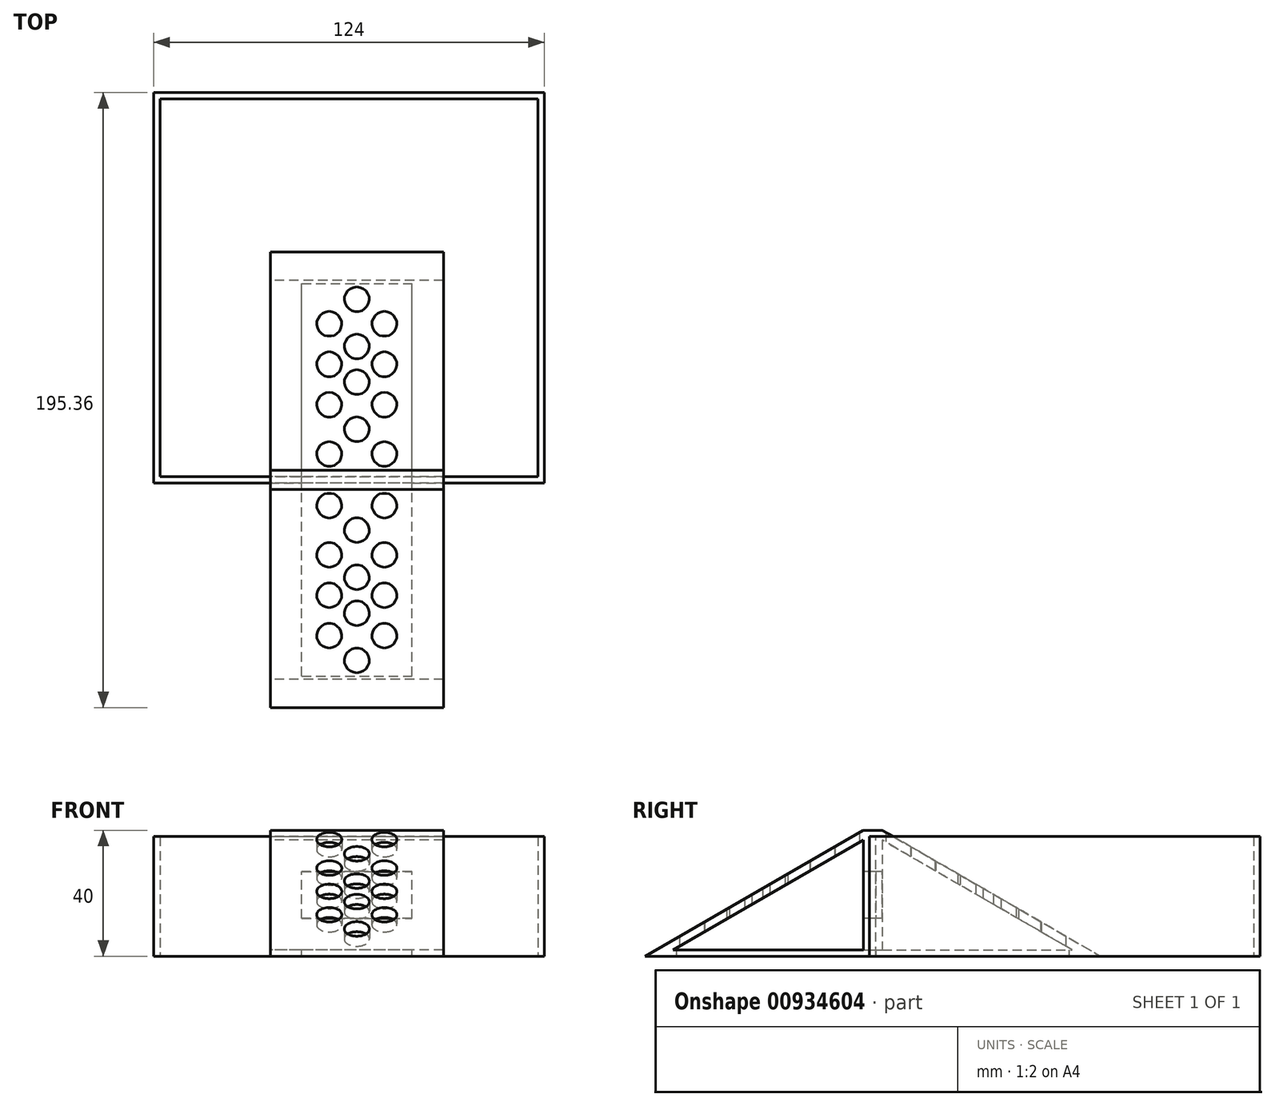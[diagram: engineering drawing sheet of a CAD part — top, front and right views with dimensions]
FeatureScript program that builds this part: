
annotation { "Feature Type Name" : "Feature", "Feature Type Description" : "" }
export const myFeature = defineFeature(function(context is Context, id is Id, definition is map)
    precondition{}
    {
        {
            var Q0;
            Q0=qCreatedBy(makeId("Top.planeOp"),FACE);
            var sketch = newSketch(context, id + "F0", { "sketchPlane" : qUnion([Q0])});
            skLineSegment(sketch, "E0.bottom", {"start": v(-60, 60) * mm, "end": v(60, 60) * mm});
            skLineSegment(sketch, "E0.top", {"start": v(-60, -60) * mm, "end": v(60, -60) * mm});
            skLineSegment(sketch, "E0.left", {"start": v(-60, 60) * mm, "end": v(-60, -60) * mm});
            skLineSegment(sketch, "E0.right", {"start": v(60, 60) * mm, "end": v(60, -60) * mm});
            skPoint(sketch, "E0.middle", {"position": v(0, 0) * mm});
            skLineSegment(sketch, "E1.bottom", {"start": v(-62, -62) * mm, "end": v(62, -62) * mm});
            skLineSegment(sketch, "E1.top", {"start": v(-62, 62) * mm, "end": v(62, 62) * mm});
            skLineSegment(sketch, "E1.left", {"start": v(-62, -62) * mm, "end": v(-62, 62) * mm});
            skLineSegment(sketch, "E1.right", {"start": v(62, -62) * mm, "end": v(62, 62) * mm});
            skSolve(sketch);
        }
        {
            var Q0;
            Q0 = qSketchRegion(id + "F0", true);
            extrude(context, id + "F1", {"entities" : qUnion([Q0]), "depth" : 38 * mm, "offsetDistance" : 25 * mm});
        }
        {
            var Q0;
            Q0=qCreatedBy(makeId("Right.planeOp"),FACE);
            var sketch = newSketch(context, id + "F2", { "sketchPlane" : qUnion([Q0])});
            skPoint(sketch, "E2.0", {"position": v(-62, 19) * mm});
            skLineSegment(sketch, "E3.0", {"start": v(-62, 38) * mm, "end": v(-62, 0) * mm, "construction": true});
            skLineSegment(sketch, "E4.0", {"start": v(-62, 38) * mm, "end": v(62, 38) * mm, "construction": true});
            skLineSegment(sketch, "E5", {"start": v(-62, 0) * mm, "end": v(-127.82, 0) * mm});
            skLineSegment(sketch, "E6", {"start": v(-124.35, 2) * mm, "end": v(-62, 38) * mm});
            skLineSegment(sketch, "E7", {"start": v(-62, 38) * mm, "end": v(-62, 0) * mm});
            skLineSegment(sketch, "E8", {"start": v(-64, 38) * mm, "end": v(-64, 2) * mm});
            skLineSegment(sketch, "E9", {"start": v(-64, 2) * mm, "end": v(-120.35, 2) * mm});
            skLineSegment(sketch, "E10.bottom", {"start": v(-62, 38) * mm, "end": v(-64.08, 38) * mm});
            skLineSegment(sketch, "E10.top", {"start": v(-62, 40) * mm, "end": v(-64.08, 40) * mm});
            skLineSegment(sketch, "E10.left", {"start": v(-62, 38) * mm, "end": v(-62, 40) * mm});
            skLineSegment(sketch, "E10.right", {"start": v(-64.08, 38) * mm, "end": v(-64.08, 40) * mm});
            skLineSegment(sketch, "E11", {"start": v(-64.08, 40) * mm, "end": v(-133.36, 0) * mm});
            skLineSegment(sketch, "E12", {"start": v(-127.82, 0) * mm, "end": v(-133.36, 0) * mm});
            skLineSegment(sketch, "E13", {"start": v(-120.35, 2) * mm, "end": v(-124.35, 2) * mm});
            skLineSegment(sketch, "E14", {"start": v(-61, 49.2) * mm, "end": v(-61, 19) * mm, "construction": true});
            skLineSegment(sketch, "E15.MirrorCS", {"start": v(-58, 38) * mm, "end": v(-58, 2) * mm});
            skLineSegment(sketch, "E16.MirrorCS", {"start": v(-60, 38) * mm, "end": v(-60, 0) * mm, "construction": true});
            skLineSegment(sketch, "E17.MirrorCS", {"start": v(2.35, 2) * mm, "end": v(-60, 38) * mm});
            skLineSegment(sketch, "E18.MirrorCS", {"start": v(-57.92, 40) * mm, "end": v(11.36, 0) * mm});
            skLineSegment(sketch, "E19.MirrorCS", {"start": v(-58, 2) * mm, "end": v(-1.65, 2) * mm});
            skLineSegment(sketch, "E20.MirrorCS", {"start": v(-60, 0) * mm, "end": v(5.82, 0) * mm});
            skLineSegment(sketch, "E21.MirrorCS", {"start": v(5.82, 0) * mm, "end": v(11.36, 0) * mm});
            skLineSegment(sketch, "E22", {"start": v(-1.65, 2) * mm, "end": v(2.35, 2) * mm});
            skLineSegment(sketch, "E23", {"start": v(11.36, 0) * mm, "end": v(-60, 0) * mm});
            skLineSegment(sketch, "E24", {"start": v(-60, 0) * mm, "end": v(-60, 40.08) * mm});
            skLineSegment(sketch, "E25", {"start": v(-57.92, 40) * mm, "end": v(-58, 38) * mm});
            skLineSegment(sketch, "E26", {"start": v(-57.92, 40) * mm, "end": v(-62, 40) * mm});
            skLineSegment(sketch, "E27", {"start": v(-60, 38) * mm, "end": v(-62, 38) * mm});
            skSolve(sketch);
        }
        {
            var Q0;
            Q0 = qSketchRegion(id + "F2", true);
            extrude(context, id + "F3", {"entities" : qUnion([Q0]), "depth" : 30 * mm, "offsetDistance" : 25 * mm, "hasSecondDirection" : true, "secondDirectionOppositeDirection" : true, "secondDirectionDepth" : 25 * mm});
        }
        {
            var Q0;
            Q0=makeQuery(id+"F3.opExtrude","SWEPT_FACE",FACE,{"disambiguationData":[OSD([sQuery(id+"F2.wireOp",EDGE,"E5"),sQuery(id+"F2.wireOp",EDGE,"E12")])]});
            var sketch = newSketch(context, id + "F4", { "sketchPlane" : qUnion([Q0])});
            skLineSegment(sketch, "E28.0", {"start": v(30, 133.36) * mm, "end": v(-25, 133.36) * mm, "construction": true});
            skLineSegment(sketch, "E29.0.0", {"start": v(-25, 60) * mm, "end": v(-25, -11.36) * mm, "construction": true});
            skLineSegment(sketch, "E29.0.1", {"start": v(-25, -11.36) * mm, "end": v(30, -11.36) * mm, "construction": true});
            skLineSegment(sketch, "E29.0.2", {"start": v(30, -11.36) * mm, "end": v(30, 60) * mm, "construction": true});
            skLineSegment(sketch, "E29.0.3", {"start": v(30, 60) * mm, "end": v(-25, 60) * mm, "construction": true});
            skLineSegment(sketch, "E30.bottom", {"start": v(-15, 123.36) * mm, "end": v(20, 123.36) * mm});
            skLineSegment(sketch, "E30.left", {"start": v(-15, 123.36) * mm, "end": v(-15, 72) * mm});
            skLineSegment(sketch, "E30.right", {"start": v(20, 123.36) * mm, "end": v(20, 72) * mm});
            skPoint(sketch, "E30.middle", {"position": v(2.5, 97.68) * mm});
            skPoint(sketch, "E30.middle.positionSnap0", {"position": v(30, 97.68) * mm});
            skPoint(sketch, "E30.middle.positionSnap1", {"position": v(2.5, 133.36) * mm});
            skPoint(sketch, "E30.centerSnap0", {"position": v(30, 97.68) * mm});
            skPoint(sketch, "E30.centerSnap1", {"position": v(2.5, 133.36) * mm});
            skLineSegment(sketch, "E31.top", {"start": v(-10.78, -1.36) * mm, "end": v(15.78, -1.36) * mm});
            skPoint(sketch, "E31.middle", {"position": v(2.5, 24.32) * mm});
            skPoint(sketch, "E31.middle.positionSnap0", {"position": v(2.5, -11.36) * mm});
            skPoint(sketch, "E31.middle.positionSnap1", {"position": v(-25, 24.32) * mm});
            skPoint(sketch, "E31.centerSnap0", {"position": v(2.5, -11.36) * mm});
            skPoint(sketch, "E31.centerSnap1", {"position": v(-25, 24.32) * mm});
            skPoint(sketch, "E31.right.start.orphan", {"position": v(15.78, 50) * mm});
            skPoint(sketch, "E31.left.start.orphan", {"position": v(-10.78, 50) * mm});
            skPoint(sketch, "E32.orphan", {"position": v(-15, -23.36) * mm});
            skPoint(sketch, "E33.orphan", {"position": v(20, -23.36) * mm});
            skLineSegment(sketch, "E34", {"start": v(-15, -1.36) * mm, "end": v(20, -1.36) * mm});
            skLineSegment(sketch, "E35.trimOffspring", {"start": v(20, 50) * mm, "end": v(20, -1.36) * mm});
            skLineSegment(sketch, "E36.trimOffspring", {"start": v(-15, 50) * mm, "end": v(-15, -1.36) * mm});
            skLineSegment(sketch, "E37", {"start": v(-15, 72) * mm, "end": v(-15, 50) * mm});
            skLineSegment(sketch, "E38", {"start": v(20, 72) * mm, "end": v(20, 50) * mm});
            skPoint(sketch, "E39.bottom.end.orphan", {"position": v(20, 72) * mm});
            skSolve(sketch);
        }
        {
            var Q0;
            Q0 = qSketchRegion(id + "F4", true);
            extrude(context, id + "F5", {"entities" : qUnion([Q0]), "operationType" : NewBodyOperationType.REMOVE, "oppositeDirection" : true, "depth" : 2 * mm, "offsetDistance" : 25 * mm});
        }
        {
            var Q0;
            Q0=makeQuery(id+"F3.opExtrude","SWEPT_FACE",FACE,{"disambiguationData":[OSD([sQuery(id+"F2.wireOp",EDGE,"E5"),sQuery(id+"F2.wireOp",EDGE,"E12")])]});
            var sketch = newSketch(context, id + "F6", { "sketchPlane" : qUnion([Q0])});
            skLineSegment(sketch, "E40", {"start": v(2.5, 133.36) * mm, "end": v(2.5, 22.72) * mm, "construction": true});
            skCircle(sketch, "E41", {"center": v(2.5, 118.36) * mm, "radius": 4 * mm});
            skCircle(sketch, "E42", {"center": v(2.5, 103.36) * mm, "radius": 4 * mm});
            skLineSegment(sketch, "E43", {"start": v(-25, 97.68) * mm, "end": v(45, 97.68) * mm, "construction": true});
            skPoint(sketch, "E44", {"position": v(2.5, 97.68) * mm});
            skLineSegment(sketch, "E45", {"start": v(2.5, 97.68) * mm, "end": v(-25, 97.68) * mm, "construction": true});
            skLineSegment(sketch, "E46", {"start": v(-11.25, 97.68) * mm, "end": v(-11.25, 79.76) * mm, "construction": true});
            skLineSegment(sketch, "E47.0", {"start": v(-15, 123.36) * mm, "end": v(20, 123.36) * mm, "construction": true});
            skLineSegment(sketch, "E48.0", {"start": v(-15, 123.36) * mm, "end": v(-15, 62) * mm, "construction": true});
            skLineSegment(sketch, "E49", {"start": v(2.5, 97.68) * mm, "end": v(-15, 123.36) * mm, "construction": true});
            skLineSegment(sketch, "E50", {"start": v(2.5, 123.36) * mm, "end": v(-15, 97.68) * mm, "construction": true});
            skCircle(sketch, "E51", {"center": v(-6.25, 110.52) * mm, "radius": 4 * mm});
            skCircle(sketch, "E52.MirrorC", {"center": v(11.25, 110.52) * mm, "radius": 4 * mm});
            skCircle(sketch, "E53.MirrorC", {"center": v(2.5, 92) * mm, "radius": 4 * mm});
            skCircle(sketch, "E54.MirrorC", {"center": v(11.25, 84.84) * mm, "radius": 4 * mm});
            skCircle(sketch, "E55.MirrorC", {"center": v(2.5, 77) * mm, "radius": 4 * mm});
            skCircle(sketch, "E56.MirrorC", {"center": v(-6.25, 84.84) * mm, "radius": 4 * mm});
            skLineSegment(sketch, "E57", {"start": v(2.5, 77) * mm, "end": v(62.89, 77) * mm, "construction": true});
            skCircle(sketch, "E58.MirrorC", {"center": v(11.25, 69.16) * mm, "radius": 4 * mm});
            skCircle(sketch, "E59.MirrorC", {"center": v(-6.25, 69.16) * mm, "radius": 4 * mm});
            skLineSegment(sketch, "E60.0.0", {"start": v(-25, 62) * mm, "end": v(-25, 60) * mm, "construction": true});
            skLineSegment(sketch, "E60.0.1", {"start": v(-25, 60) * mm, "end": v(30, 60) * mm, "construction": true});
            skLineSegment(sketch, "E60.0.2", {"start": v(30, 60) * mm, "end": v(30, 62) * mm, "construction": true});
            skLineSegment(sketch, "E60.0.3", {"start": v(30, 62) * mm, "end": v(-25, 62) * mm, "construction": true});
            skLineSegment(sketch, "E61", {"start": v(30, 61) * mm, "end": v(23.41, 61) * mm, "construction": true});
            skCircle(sketch, "E62.MirrorC", {"center": v(11.25, 52.84) * mm, "radius": 4 * mm});
            skCircle(sketch, "E63.MirrorC", {"center": v(2.5, 45) * mm, "radius": 4 * mm});
            skCircle(sketch, "E64.MirrorC", {"center": v(-6.25, 52.84) * mm, "radius": 4 * mm});
            skCircle(sketch, "E65.MirrorC", {"center": v(11.25, 37.16) * mm, "radius": 4 * mm});
            skCircle(sketch, "E66.MirrorC", {"center": v(-6.25, 37.16) * mm, "radius": 4 * mm});
            skCircle(sketch, "E67.MirrorC", {"center": v(2.5, 30) * mm, "radius": 4 * mm});
            skCircle(sketch, "E68.MirrorC", {"center": v(2.5, 18.64) * mm, "radius": 4 * mm});
            skCircle(sketch, "E69.MirrorC", {"center": v(11.25, 11.48) * mm, "radius": 4 * mm});
            skCircle(sketch, "E70.MirrorC", {"center": v(2.5, 3.64) * mm, "radius": 4 * mm});
            skCircle(sketch, "E71.MirrorC", {"center": v(-6.25, 11.48) * mm, "radius": 4 * mm});
            skCircle(sketch, "E72", {"center": v(-6.25, 97.68) * mm, "radius": 4 * mm});
            skCircle(sketch, "E73.MirrorC", {"center": v(11.25, 97.68) * mm, "radius": 4 * mm});
            skCircle(sketch, "E74.MirrorC", {"center": v(-6.25, 24.32) * mm, "radius": 4 * mm});
            skCircle(sketch, "E75.MirrorC", {"center": v(11.25, 24.32) * mm, "radius": 4 * mm});
            skSolve(sketch);
        }
        {
            var Q0;
            Q0 = qSketchRegion(id + "F6", true);
            extrude(context, id + "F7", {"entities" : qUnion([Q0]), "operationType" : NewBodyOperationType.REMOVE, "oppositeDirection" : true, "depth" : 70 * mm, "offsetDistance" : 25 * mm});
        }
        {
            var Q0;
            Q0=makeQuery(id+"F3.opExtrude","SWEPT_FACE",FACE,{"disambiguationData":[OSD([sQuery(id+"F2.wireOp",EDGE,"E8")])]});
            var sketch = newSketch(context, id + "F8", { "sketchPlane" : qUnion([Q0])});
            skLineSegment(sketch, "E76.0.0", {"start": v(-25, 36.85) * mm, "end": v(-25, 2) * mm, "construction": true});
            skLineSegment(sketch, "E76.0.1", {"start": v(-25, 2) * mm, "end": v(-15, 2) * mm, "construction": true});
            skLineSegment(sketch, "E76.0.2", {"start": v(-15, 2) * mm, "end": v(20, 2) * mm, "construction": true});
            skLineSegment(sketch, "E76.0.3", {"start": v(20, 2) * mm, "end": v(30, 2) * mm, "construction": true});
            skLineSegment(sketch, "E76.0.4", {"start": v(30, 2) * mm, "end": v(30, 36.85) * mm, "construction": true});
            skLineSegment(sketch, "E76.0.5", {"start": v(30, 36.85) * mm, "end": v(-25, 36.85) * mm, "construction": true});
            skLineSegment(sketch, "E77.bottom", {"start": v(-15, 26.85) * mm, "end": v(20, 26.85) * mm});
            skLineSegment(sketch, "E77.top", {"start": v(-15, 12) * mm, "end": v(20, 12) * mm});
            skLineSegment(sketch, "E77.left", {"start": v(-15, 26.85) * mm, "end": v(-15, 12) * mm});
            skLineSegment(sketch, "E77.right", {"start": v(20, 26.85) * mm, "end": v(20, 12) * mm});
            skPoint(sketch, "E77.middle", {"position": v(2.5, 19.42) * mm});
            skPoint(sketch, "E77.middle.positionSnap0", {"position": v(-25, 19.42) * mm});
            skPoint(sketch, "E77.middle.positionSnap1", {"position": v(2.5, 36.85) * mm});
            skPoint(sketch, "E77.centerSnap0", {"position": v(-25, 19.42) * mm});
            skPoint(sketch, "E77.centerSnap1", {"position": v(2.5, 36.85) * mm});
            skSolve(sketch);
        }
        {
            var Q0;
            Q0 = qSketchRegion(id + "F8", true);
            extrude(context, id + "F9", {"entities" : qUnion([Q0]), "operationType" : NewBodyOperationType.REMOVE, "oppositeDirection" : true, "depth" : 10 * mm, "offsetDistance" : 25 * mm});
        }
    });
